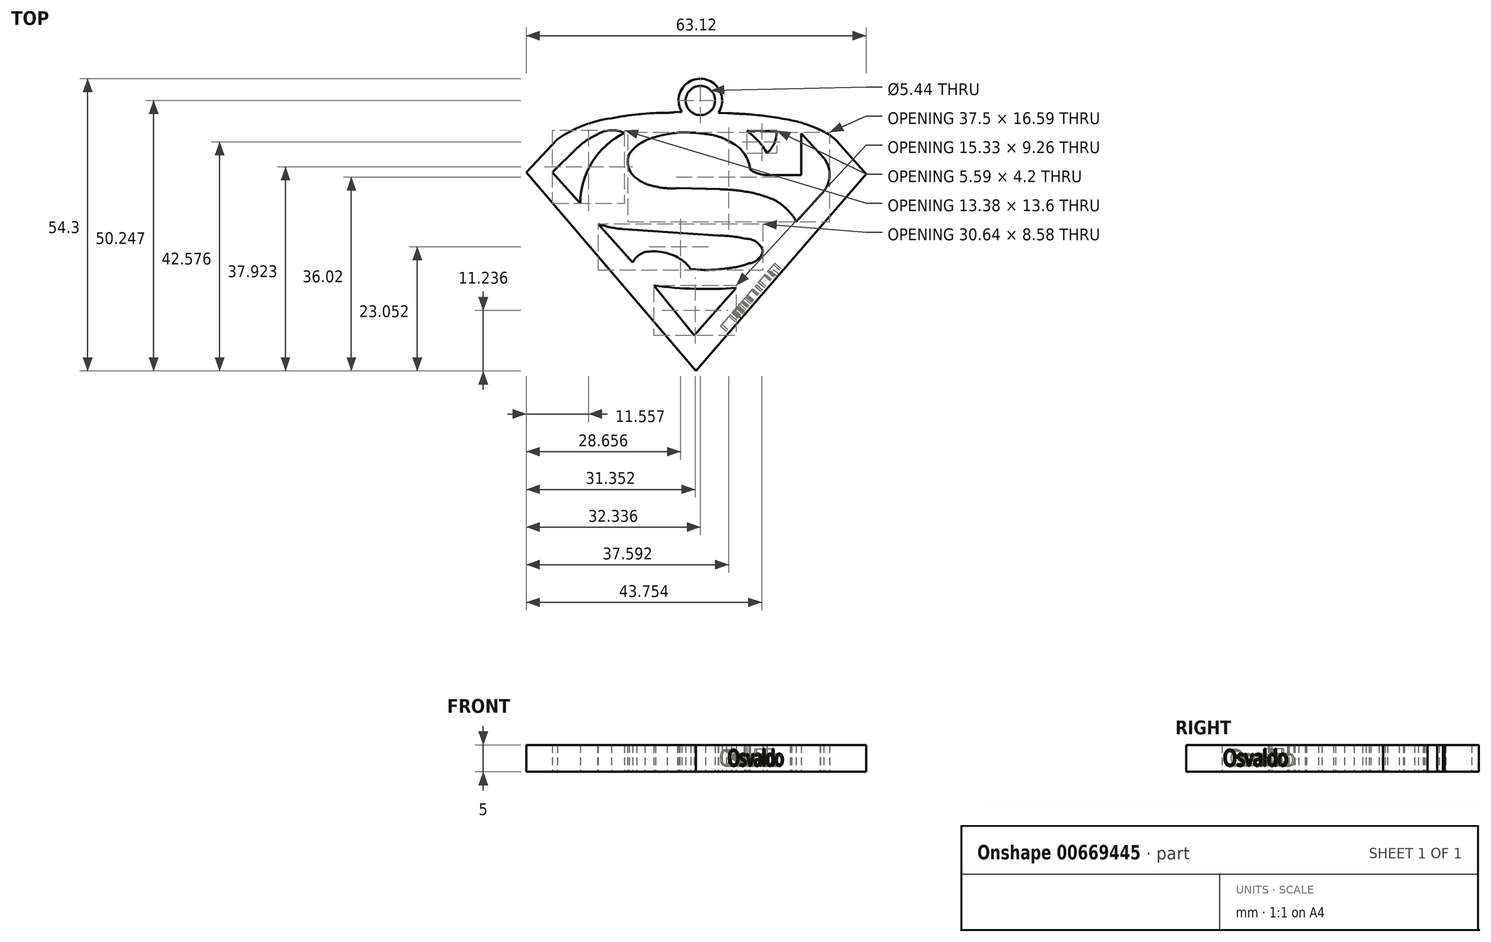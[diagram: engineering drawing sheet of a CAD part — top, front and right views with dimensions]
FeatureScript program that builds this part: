
annotation { "Feature Type Name" : "Feature", "Feature Type Description" : "" }
export const myFeature = defineFeature(function(context is Context, id is Id, definition is map)
    precondition{}
    {
        {
            var Q0;
            Q0=qCreatedBy(makeId("Top.planeOp"),FACE);
            var sketch = newSketch(context, id + "F0", { "sketchPlane" : qUnion([Q0])});
            skArc(sketch, "E0", {"start": v(23.43, 23) * mm, "mid": v(22.07, 22.26) * mm, "end": v(21.1, 21.05) * mm});
            skArc(sketch, "E1", {"start": v(29.9, 21.76) * mm, "mid": v(26.78, 22.97) * mm, "end": v(23.43, 23) * mm});
            skArc(sketch, "E2", {"start": v(31.89, 19.84) * mm, "mid": v(31, 20.9) * mm, "end": v(29.9, 21.76) * mm});
            skArc(sketch, "E3", {"start": v(31.89, 19.84) * mm, "mid": v(35.22, 19.68) * mm, "end": v(38.55, 19.98) * mm});
            skArc(sketch, "E4", {"start": v(38.55, 19.98) * mm, "mid": v(40.67, 20.28) * mm, "end": v(42.72, 20.9) * mm});
            skArc(sketch, "E5", {"start": v(42.72, 20.9) * mm, "mid": v(44.39, 21.65) * mm, "end": v(45.34, 23.21) * mm});
            skArc(sketch, "E6", {"start": v(45.34, 23.21) * mm, "mid": v(44.06, 24.9) * mm, "end": v(42.02, 25.47) * mm});
            skArc(sketch, "E7", {"start": v(42.02, 25.47) * mm, "mid": v(39.53, 25.9) * mm, "end": v(37.01, 26.07) * mm});
            skLineSegment(sketch, "E8", {"start": v(37.01, 26.07) * mm, "end": v(19.3, 27.28) * mm});
            skArc(sketch, "E9", {"start": v(14.7, 28.25) * mm, "mid": v(16.96, 27.6) * mm, "end": v(19.3, 27.28) * mm});
            skLineSegment(sketch, "E10", {"start": v(14.7, 28.25) * mm, "end": v(21.1, 21.05) * mm});
            skArc(sketch, "E11", {"start": v(19.6, 45.13) * mm, "mid": v(13.62, 39.76) * mm, "end": v(11.39, 32.03) * mm});
            skArc(sketch, "E12", {"start": v(19.6, 45.13) * mm, "mid": v(17.05, 45.64) * mm, "end": v(14.57, 44.86) * mm});
            skArc(sketch, "E13", {"start": v(14.57, 44.86) * mm, "mid": v(12.57, 43.75) * mm, "end": v(10.8, 42.3) * mm});
            skLineSegment(sketch, "E14", {"start": v(10.8, 42.3) * mm, "end": v(6.23, 37.81) * mm});
            skLineSegment(sketch, "E15", {"start": v(6.23, 37.81) * mm, "end": v(11.39, 32.03) * mm});
            skArc(sketch, "E16", {"start": v(46.07, 41.38) * mm, "mid": v(44.42, 43.66) * mm, "end": v(42.32, 45.52) * mm});
            skArc(sketch, "E17", {"start": v(46.07, 41.38) * mm, "mid": v(47.44, 43.29) * mm, "end": v(47.9, 45.59) * mm});
            skLineSegment(sketch, "E18", {"start": v(47.9, 45.59) * mm, "end": v(42.32, 45.52) * mm});
            skLineSegment(sketch, "E19", {"start": v(52.4, 45.02) * mm, "end": v(52.4, 37.29) * mm});
            skLineSegment(sketch, "E20", {"start": v(52.4, 37.29) * mm, "end": v(46.34, 37.29) * mm});
            skArc(sketch, "E21", {"start": v(42.98, 38.28) * mm, "mid": v(44.59, 37.54) * mm, "end": v(46.34, 37.29) * mm});
            skArc(sketch, "E22", {"start": v(42.98, 38.28) * mm, "mid": v(41.87, 41.27) * mm, "end": v(39.44, 43.32) * mm});
            skArc(sketch, "E23", {"start": v(39.44, 43.32) * mm, "mid": v(37.13, 44.44) * mm, "end": v(34.62, 44.94) * mm});
            skArc(sketch, "E24", {"start": v(34.62, 44.94) * mm, "mid": v(32.19, 45.19) * mm, "end": v(29.74, 45.21) * mm});
            skArc(sketch, "E25", {"start": v(29.74, 45.21) * mm, "mid": v(26.98, 44.8) * mm, "end": v(24.3, 44.05) * mm});
            skArc(sketch, "E26", {"start": v(24.3, 44.05) * mm, "mid": v(22.17, 42.93) * mm, "end": v(20.47, 41.22) * mm});
            skArc(sketch, "E27", {"start": v(20.47, 41.22) * mm, "mid": v(20.37, 38.69) * mm, "end": v(21.9, 36.67) * mm});
            skArc(sketch, "E28", {"start": v(21.9, 36.67) * mm, "mid": v(23.52, 35.7) * mm, "end": v(25.35, 35.18) * mm});
            skArc(sketch, "E29", {"start": v(25.35, 35.18) * mm, "mid": v(27.37, 34.86) * mm, "end": v(29.42, 34.86) * mm});
            skLineSegment(sketch, "E30", {"start": v(29.42, 34.86) * mm, "end": v(33.89, 34.75) * mm});
            skLineSegment(sketch, "E31", {"start": v(33.89, 34.75) * mm, "end": v(37.31, 34.67) * mm});
            skArc(sketch, "E32", {"start": v(41.82, 34.27) * mm, "mid": v(39.57, 34.54) * mm, "end": v(37.31, 34.67) * mm});
            skArc(sketch, "E33", {"start": v(46.8, 32.95) * mm, "mid": v(44.35, 33.76) * mm, "end": v(41.82, 34.27) * mm});
            skArc(sketch, "E34", {"start": v(50.39, 30.25) * mm, "mid": v(48.77, 31.84) * mm, "end": v(46.8, 32.95) * mm});
            skArc(sketch, "E35", {"start": v(51.47, 28.64) * mm, "mid": v(51, 29.5) * mm, "end": v(50.39, 30.25) * mm});
            skLineSegment(sketch, "E36", {"start": v(51.47, 28.64) * mm, "end": v(56, 33.65) * mm});
            skArc(sketch, "E37", {"start": v(56, 33.65) * mm, "mid": v(57.7, 36.93) * mm, "end": v(56.61, 40.47) * mm});
            skLineSegment(sketch, "E38", {"start": v(56.61, 40.47) * mm, "end": v(52.4, 45.02) * mm});
            skLineSegment(sketch, "E39", {"start": v(1.36, 37.83) * mm, "end": v(32.9, 0.9) * mm});
            skLineSegment(sketch, "E40", {"start": v(32.9, 0.9) * mm, "end": v(64.48, 37.48) * mm});
            skLineSegment(sketch, "E41", {"start": v(64.48, 37.48) * mm, "end": v(59.3, 43.32) * mm});
            skLineSegment(sketch, "E42", {"start": v(1.36, 37.83) * mm, "end": v(7.15, 43.99) * mm});
            skArc(sketch, "E43", {"start": v(17.15, 47.86) * mm, "mid": v(11.92, 46.52) * mm, "end": v(7.15, 43.99) * mm});
            skArc(sketch, "E44", {"start": v(27.54, 48.86) * mm, "mid": v(22.32, 48.63) * mm, "end": v(17.15, 47.86) * mm});
            skArc(sketch, "E45", {"start": v(43.44, 48.54) * mm, "mid": v(41.07, 48.7) * mm, "end": v(38.7, 48.8) * mm});
            skArc(sketch, "E46", {"start": v(50.65, 47.48) * mm, "mid": v(47.06, 48.1) * mm, "end": v(43.44, 48.54) * mm});
            skArc(sketch, "E47", {"start": v(55.9, 45.72) * mm, "mid": v(53.33, 46.75) * mm, "end": v(50.65, 47.48) * mm});
            skArc(sketch, "E48", {"start": v(59.3, 43.32) * mm, "mid": v(57.75, 44.72) * mm, "end": v(55.9, 45.72) * mm});
            skArc(sketch, "E49.trimOffspring", {"start": v(28.93, 48.97) * mm, "mid": v(28.23, 48.92) * mm, "end": v(27.54, 48.86) * mm});
            skPoint(sketch, "E50.orphan", {"position": v(35.4, 48.86) * mm});
            skArc(sketch, "E51", {"start": v(37.03, 48.86) * mm, "mid": v(33.81, 55.2) * mm, "end": v(30.23, 49.06) * mm});
            skCircle(sketch, "E52", {"center": v(33.7, 51.16) * mm, "radius": 2.72 * mm});
            skLineSegment(sketch, "E53", {"start": v(28.93, 48.97) * mm, "end": v(30.23, 49.06) * mm});
            skLineSegment(sketch, "E54", {"start": v(38.7, 48.8) * mm, "end": v(37.03, 48.86) * mm});
            skLineSegment(sketch, "E55", {"start": v(25.05, 16.78) * mm, "end": v(32.55, 7.51) * mm});
            skLineSegment(sketch, "E56", {"start": v(32.55, 7.51) * mm, "end": v(40.38, 16.35) * mm});
            skArc(sketch, "E57", {"start": v(25.05, 16.78) * mm, "mid": v(32.7, 16.17) * mm, "end": v(40.38, 16.35) * mm});
            skSolve(sketch);
        }
        {
            var Q0;
            Q0 = qSketchRegion(id + "F0", true);
            extrude(context, id + "F1", {"entities" : qUnion([Q0]), "depth" : 5 * mm, "offsetDistance" : 25 * mm});
        }
        {
            var Q0;
            Q0=makeQuery(id+"F1.opExtrude","SWEPT_FACE",FACE,{"disambiguationData":[OSD([sQuery(id+"F0.wireOp",EDGE,"E40")])]});
            var sketch = newSketch(context, id + "F2", { "sketchPlane" : qUnion([Q0])});
            skText(sketch, "E58", { "text": "Osvaldo ", "fontName": "OpenSans-Regular.ttf"});
            const initialGuessF2  = {"E58": [0.03125, 0.0011, 1, 0, 0.00302]};
            skSetInitialGuess(sketch, initialGuessF2);
            skSolve(sketch);
        }
        {
            var Q0;
            Q0 = qSketchRegion(id + "F2", true);
            extrude(context, id + "F3", {"entities" : qUnion([Q0]), "operationType" : NewBodyOperationType.REMOVE, "oppositeDirection" : true, "depth" : 2 * mm, "offsetDistance" : 25 * mm});
        }
    });
